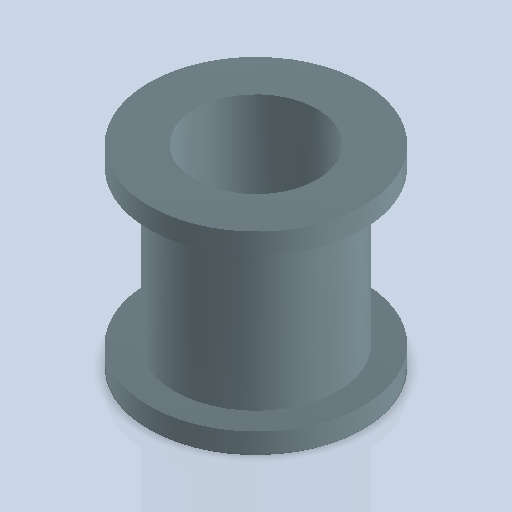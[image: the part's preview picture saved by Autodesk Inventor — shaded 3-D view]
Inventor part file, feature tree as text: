
AUTODESK INVENTOR PART (.ipt)
format: ipt  version: 2024 (Build 280153000, 153)  size: 237,568 bytes
history: native  units: mm
features: sketch x3, hole x2, revolve x1, plane x1
ambient origin geometry x8: Origin, YZ Plane, XZ Plane, XY Plane, X Axis, Y Axis, Z Axis, Center Point
bodies: Volumenkörper1 (feature_tree)
feature tree (7):
  revolve  "Umdrehung1"
  hole  "Bohrung1"  [1 undecoded]
  plane  "Arbeitsebene1"
  hole  "Bohrung2"  [1 undecoded]
  sketch  "Skizze1"  dims[d0=2.0mm d1=2.0mm]
  sketch  "Skizze2"  dims[d2=21.0mm d3=16.0mm]
  sketch  "Skizze3"  dims[d4=19.0mm d5=90.0deg d6=12.0mm d7=6.0mm d8=4.0mm d9=2.0mm d10=90.0deg d11=8.0mm d12=20.594885mm d13=8.0mm d14=9.5mm d15=3.0mm d16=6.0mm d17=4.0mm d18=2.0mm d19=90.0deg d20=5.0mm d21=0.0mm]
note: 2 required parameter values undecoded (feature->parameter linkage not recoverable at this tier; creation-order binding heuristic only, values carry confidence <= 0.55)
